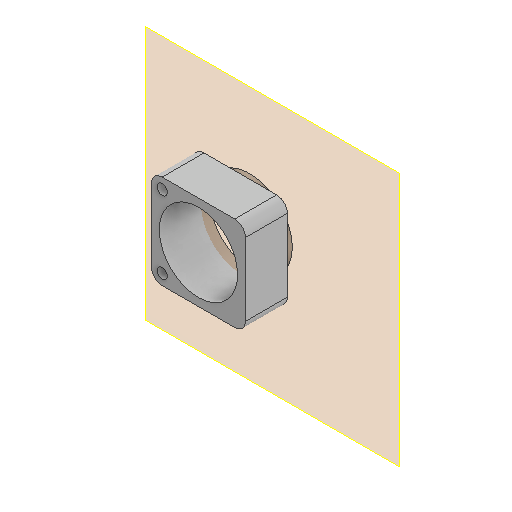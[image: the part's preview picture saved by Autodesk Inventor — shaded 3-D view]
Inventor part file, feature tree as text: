
AUTODESK INVENTOR PART (.ipt)
format: ipt  version: 2022 (Build 260153000, 153)  size: 155,136 bytes
history: native  units: in
note: dims shown in document units (in); Inventor stores cm internally (conversion verified against a paired STEP export)
features: reference x8, other x7, sketch x3, extrude x2, plane x1, hole x1, projected_geometry x1
ambient origin geometry x8: Origin, YZ Plane, XZ Plane, XY Plane, X Axis, Y Axis, Z Axis, Center Point
bodies: Solid1 (feature_tree)
feature tree (23):
  plane  "Work Plane1"
  extrude  "Extrusion1"  Depth=0.0039in
  hole  "Hole1"  [1 undecoded]
  extrude  "Extrusion2"  [1 undecoded]
  sketch  "Sketch1"  dims[d0=0.3543in d1=0.0in]
  reference  "Reference1"
  reference  "Reference2"
  reference  "Reference3"
  reference  "Reference4"
  reference  "Reference5"
  reference  "Reference6"
  sketch  "Sketch2"  dims[d2=0.0866in d3=0.75in d4=0.375in d5=0.25in d6=0.5635in d7=0.5906in d8=0.8108in d10=0.0039in]
  reference  "Reference7"
  projected_geometry  "Projected Loop1"
  sketch  "Sketch3"  dims[d11=0.0787in d12=0.0in]
  reference  "Reference8"
  other  "<userpath>\Documents\UC2-INVENTOR-Git\uc2_v3\Assembly_Cube_SQUID_Z_Focus_v3.iam"
  other  "Assembly_Cube_SQUID_Z_Focus_v3.iam"
  other  "30_Cube_SQUID_Z_Focus_base_v3:1"
  other  "<userpath> Lab\Documents\UC2-INVENTOR-Git\uc2_v3\Assembly_Cube_SQUID_Z_Focus_v3.iam"
  other  "AMETEK-21H4U-2_5-0_75-12-ENC:1"
  other  "Assembly_Cube_empty_IM_v3:1"
  other  "10_Cube_1x1_IM:2"
note: 2 required parameter values undecoded (feature->parameter linkage not recoverable at this tier; creation-order binding heuristic only, values carry confidence <= 0.55)
